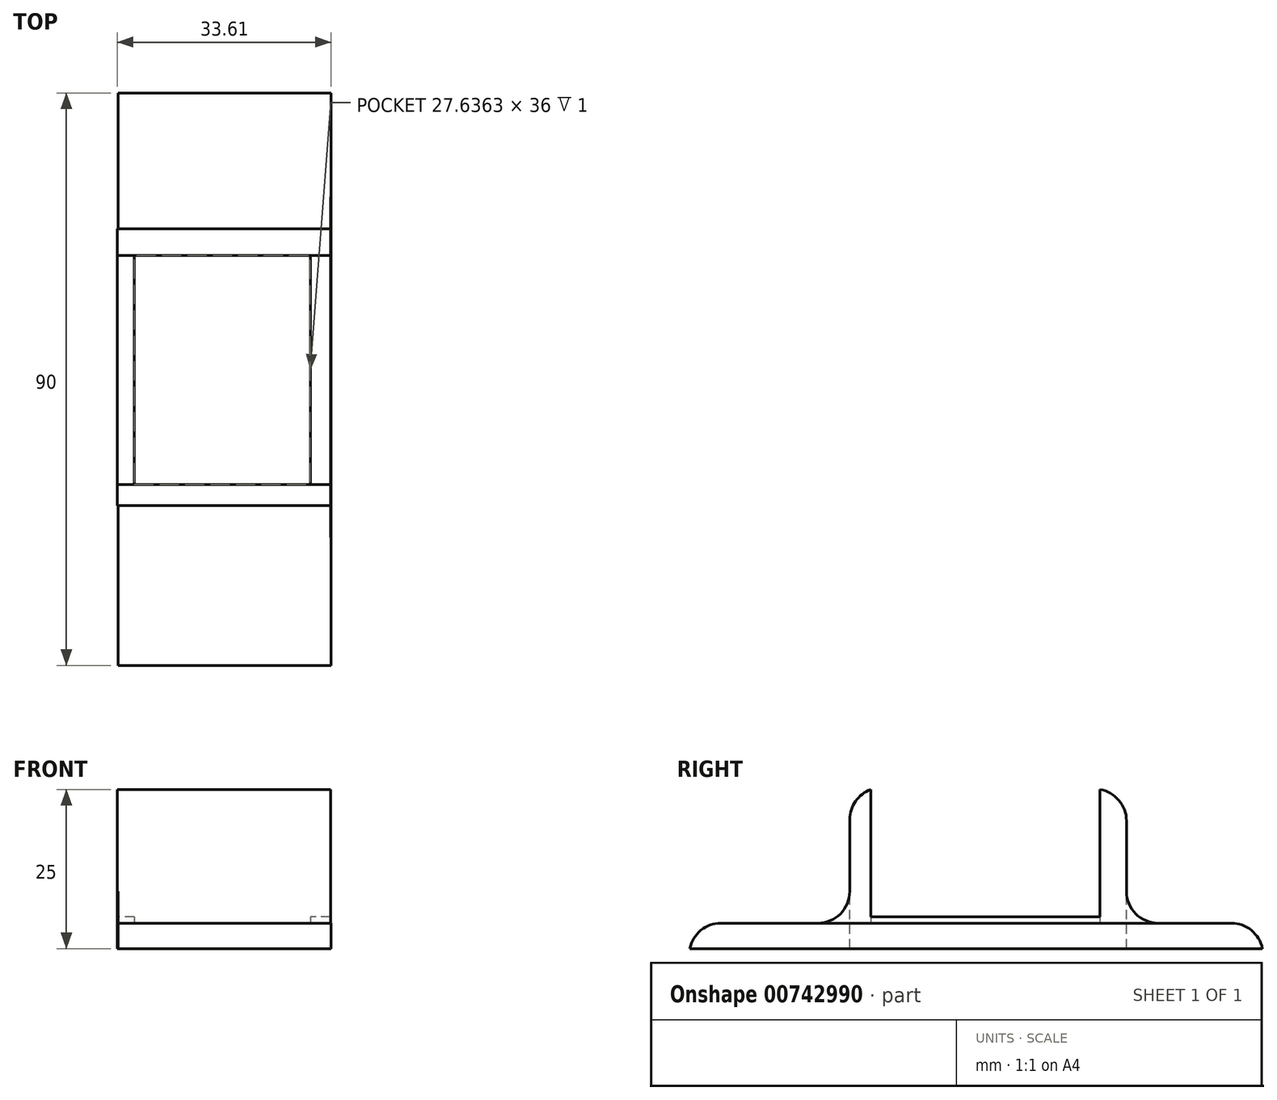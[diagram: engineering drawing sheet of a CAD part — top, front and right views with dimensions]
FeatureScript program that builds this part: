
annotation { "Feature Type Name" : "Feature", "Feature Type Description" : "" }
export const myFeature = defineFeature(function(context is Context, id is Id, definition is map)
    precondition{}
    {
        {
            var Q0;
            Q0=qCreatedBy(makeId("Top.planeOp"),FACE);
            var sketch = newSketch(context, id + "F0", { "sketchPlane" : qUnion([Q0])});
            skLineSegment(sketch, "E0.bottom", {"start": v(-49.8, 18.99) * mm, "end": v(-22.16, 18.99) * mm});
            skLineSegment(sketch, "E0.top", {"start": v(-49.8, -17.01) * mm, "end": v(-22.16, -17.01) * mm});
            skLineSegment(sketch, "E0.left", {"start": v(-49.8, 18.99) * mm, "end": v(-49.8, -17.01) * mm});
            skLineSegment(sketch, "E0.right", {"start": v(-22.16, 18.99) * mm, "end": v(-22.16, -17.01) * mm});
            skSolve(sketch);
        }
        {
            var Q0;
            Q0=qCreatedBy(makeId("Top.planeOp"),FACE);
            var sketch = newSketch(context, id + "F1", { "sketchPlane" : qUnion([Q0])});
            skLineSegment(sketch, "E1.bottom", {"start": v(-52.48, -20.32) * mm, "end": v(-18.97, -20.32) * mm});
            skLineSegment(sketch, "E1.top", {"start": v(-52.48, 23.18) * mm, "end": v(-18.97, 23.18) * mm});
            skLineSegment(sketch, "E1.left", {"start": v(-52.48, -20.32) * mm, "end": v(-52.48, 23.18) * mm});
            skLineSegment(sketch, "E1.right", {"start": v(-18.97, -20.32) * mm, "end": v(-18.97, 23.18) * mm});
            skSolve(sketch);
        }
        {
            var Q0;
            Q0 = qSketchRegion(id + "F1", true);
            extrude(context, id + "F2", {"entities" : qUnion([Q0]), "depth" : 25 * mm, "offsetDistance" : 25 * mm});
        }
        {
            var Q0;
            Q0 = qSketchRegion(id + "F0", true);
            extrude(context, id + "F3", {"entities" : qUnion([Q0]), "operationType" : NewBodyOperationType.REMOVE, "depth" : 25 * mm, "offsetDistance" : 25 * mm});
        }
        {
            var Q0;
            Q0=makeQuery(id+"F2.opExtrude","CAP_FACE",FACE,{"disambiguationData":[OSD([sQuery(id+"F1.wireOp",EDGE,"E1.bottom"),sQuery(id+"F1.wireOp",EDGE,"E1.top"),sQuery(id+"F1.wireOp",EDGE,"E1.left"),sQuery(id+"F1.wireOp",EDGE,"E1.right")])],"isStart":false});
            var sketch = newSketch(context, id + "F4", { "sketchPlane" : qUnion([Q0])});
            skLineSegment(sketch, "E2.bottom", {"start": v(-18.97, 18.99) * mm, "end": v(-52.48, 18.99) * mm});
            skLineSegment(sketch, "E2.top", {"start": v(-18.97, -17.01) * mm, "end": v(-52.48, -17.01) * mm});
            skLineSegment(sketch, "E2.left", {"start": v(-18.97, 18.99) * mm, "end": v(-18.97, -17.01) * mm});
            skLineSegment(sketch, "E2.right", {"start": v(-52.48, 18.99) * mm, "end": v(-52.48, -17.01) * mm});
            skSolve(sketch);
        }
        {
            var Q0;
            Q0 = qSketchRegion(id + "F4", true);
            extrude(context, id + "F5", {"entities" : qUnion([Q0]), "operationType" : NewBodyOperationType.REMOVE, "oppositeDirection" : true, "depth" : 20 * mm, "offsetDistance" : 25 * mm});
        }
        {
            var Q0;
            Q0=makeQuery(id+"F2.opExtrude","CAP_EDGE",EDGE,{"disambiguationData":[OSD([sQuery(id+"F1.wireOp",EDGE,"E1.top")])],"isStart":false});
            var Q1;
            Q1=makeQuery(id+"F2.opExtrude","CAP_EDGE",EDGE,{"disambiguationData":[OSD([sQuery(id+"F1.wireOp",EDGE,"E1.bottom")])],"isStart":false});
            fillet(context, id + "F6", {"entities" : qUnion([Q0, Q1]), "radius" : 5 * mm, "tangentPropagation" : true, "allowEdgeOverflow" : false});
        }
        {
            var Q0;
            Q0=qCreatedBy(makeId("Top.planeOp"),FACE);
            var sketch = newSketch(context, id + "F7", { "sketchPlane" : qUnion([Q0])});
            skLineSegment(sketch, "E3.bottom", {"start": v(-52.37, -45.46) * mm, "end": v(-18.37, -45.46) * mm});
            skLineSegment(sketch, "E3.top", {"start": v(-52.37, 44.54) * mm, "end": v(-18.37, 44.54) * mm});
            skLineSegment(sketch, "E3.left", {"start": v(-52.37, -45.46) * mm, "end": v(-52.37, 44.54) * mm});
            skLineSegment(sketch, "E3.right", {"start": v(-18.37, -45.46) * mm, "end": v(-18.37, 44.54) * mm});
            skSolve(sketch);
        }
        {
            var Q0;
            Q0 = qSketchRegion(id + "F7", true);
            extrude(context, id + "F8", {"entities" : qUnion([Q0]), "operationType" : NewBodyOperationType.ADD, "depth" : 4 * mm, "offsetDistance" : 25 * mm});
        }
        {
            var Q0;
            Q0=makeQuery(id+"F8.opExtrude","CAP_EDGE",EDGE,{"disambiguationData":[OSD([sQuery(id+"F7.wireOp",EDGE,"E3.bottom")])],"isStart":false});
            var Q1;
            Q1=makeQuery(id+"F8.opExtrude","CAP_EDGE",EDGE,{"disambiguationData":[OSD([sQuery(id+"F7.wireOp",EDGE,"E3.top")])],"isStart":false});
            fillet(context, id + "F9", {"entities" : qUnion([Q0, Q1]), "radius" : 5 * mm, "tangentPropagation" : true, "allowEdgeOverflow" : false});
        }
        {
            var Q0;
            Q0=makeQuery(id+"F8.boolean.opBoolean","INTERSECT",EDGE,{"derivedFrom":[makeQuery(id+"F2.opExtrude","SWEPT_FACE",FACE,{"disambiguationData":[OSD([sQuery(id+"F1.wireOp",EDGE,"E1.bottom")])]}),makeQuery(id+"F8.opExtrude","CAP_FACE",FACE,{"disambiguationData":[OSD([sQuery(id+"F7.wireOp",EDGE,"E3.bottom"),sQuery(id+"F7.wireOp",EDGE,"E3.top"),sQuery(id+"F7.wireOp",EDGE,"E3.left"),sQuery(id+"F7.wireOp",EDGE,"E3.right")])],"isStart":false})]});
            var Q1;
            Q1=makeQuery(id+"F8.boolean.opBoolean","INTERSECT",EDGE,{"derivedFrom":[makeQuery(id+"F2.opExtrude","SWEPT_FACE",FACE,{"disambiguationData":[OSD([sQuery(id+"F1.wireOp",EDGE,"E1.top")])]}),makeQuery(id+"F8.opExtrude","CAP_FACE",FACE,{"disambiguationData":[OSD([sQuery(id+"F7.wireOp",EDGE,"E3.bottom"),sQuery(id+"F7.wireOp",EDGE,"E3.top"),sQuery(id+"F7.wireOp",EDGE,"E3.left"),sQuery(id+"F7.wireOp",EDGE,"E3.right")])],"isStart":false})]});
            fillet(context, id + "F10", {"entities" : qUnion([Q0, Q1]), "radius" : 5 * mm, "tangentPropagation" : true, "allowEdgeOverflow" : false});
        }
        {
            var Q0;
            Q0=makeQuery(id+"F8.opExtrude","SWEPT_FACE",FACE,{"disambiguationData":[OSD([sQuery(id+"F7.wireOp",EDGE,"E3.right")])]});
            extrude(context, id + "F11", {"entities" : qUnion([Q0]), "operationType" : NewBodyOperationType.REMOVE, "oppositeDirection" : true, "depth" : 0.5 * mm, "offsetDistance" : 25 * mm});
        }
    });
